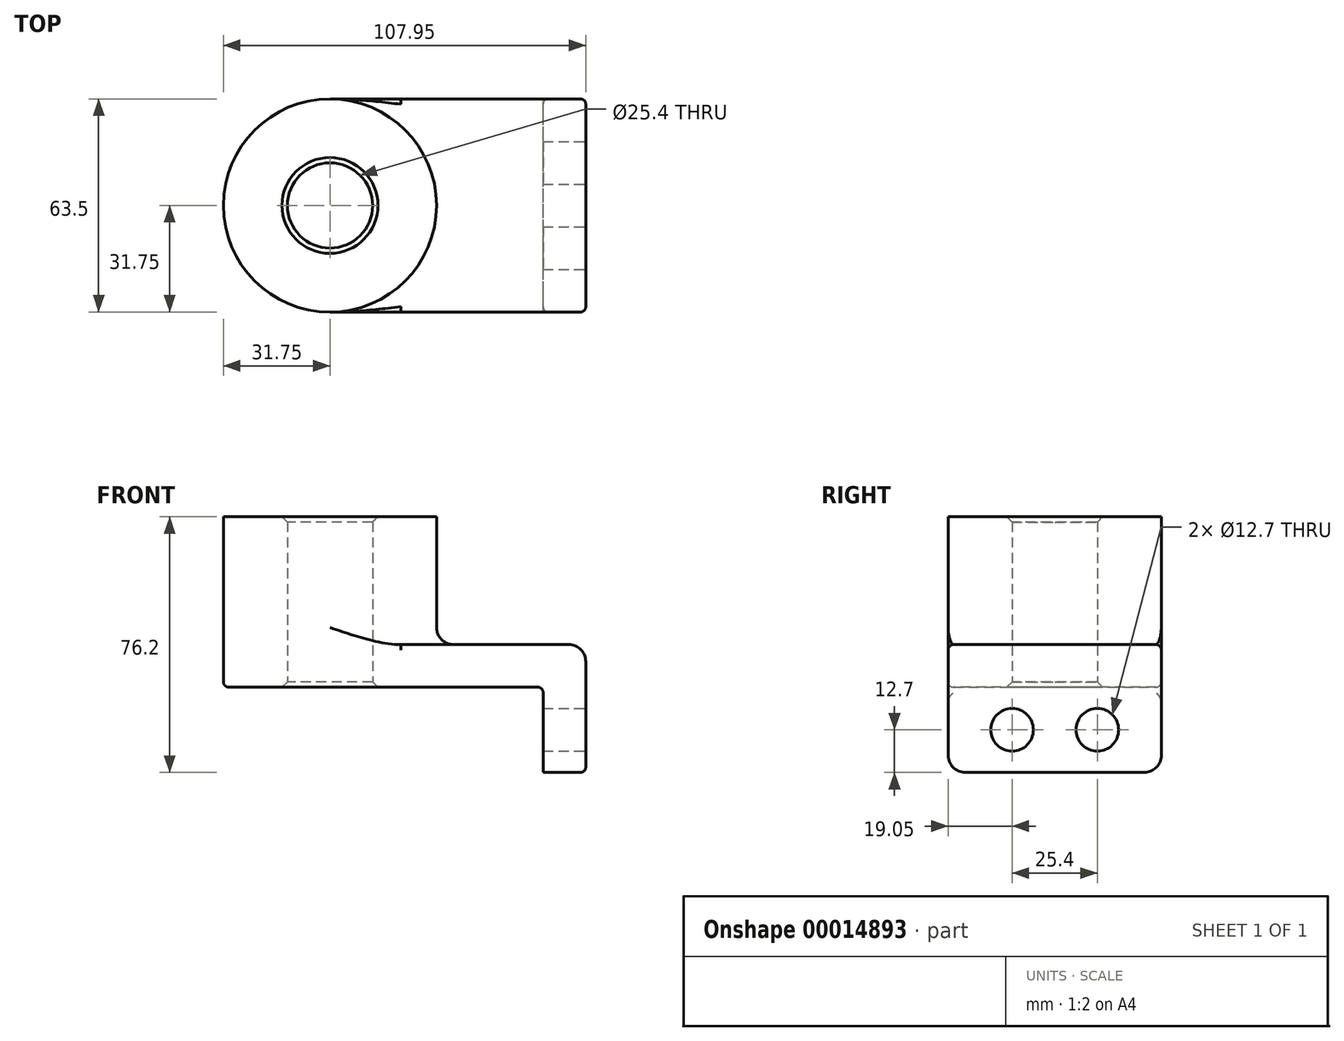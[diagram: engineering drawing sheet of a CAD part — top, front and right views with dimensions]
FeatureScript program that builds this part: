
annotation { "Feature Type Name" : "Feature", "Feature Type Description" : "" }
export const myFeature = defineFeature(function(context is Context, id is Id, definition is map)
    precondition{}
    {
        {
            var Q0;
            Q0=qCreatedBy(makeId("Top.planeOp"),FACE);
            var sketch = newSketch(context, id + "F0", { "sketchPlane" : qUnion([Q0])});
            skLineSegment(sketch, "E0.rect.bottom", {"start": v(-38.1, 31.75) * mm, "end": v(38.1, 31.75) * mm});
            skLineSegment(sketch, "E0.rect.top", {"start": v(-38.1, -31.75) * mm, "end": v(38.1, -31.75) * mm});
            skLineSegment(sketch, "E0.rect.left", {"start": v(-38.1, 31.75) * mm, "end": v(-38.1, -31.75) * mm});
            skLineSegment(sketch, "E0.rect.right", {"start": v(38.1, 31.75) * mm, "end": v(38.1, -31.75) * mm});
            skPoint(sketch, "E0.rect.middle", {"position": v(0, 0) * mm});
            skCircle(sketch, "E1", {"center": v(-38.1, 0) * mm, "radius": 31.75 * mm});
            skCircle(sketch, "E2", {"center": v(-38.1, 0) * mm, "radius": 12.7 * mm});
            skSolve(sketch);
        }
        {
            var Q0;
            Q0 = qSketchRegion(id + "F0", true);
            extrude(context, id + "F1", {"entities" : qUnion([Q0]), "depth" : 12.7 * mm});
        }
        {
            var Q0;
            {var subQ0=sQuery(id+"F0.wireOp",EDGE,"E2");var subQ1=sQuery(id+"F0.wireOp",EDGE,"E0.rect.left");var subQ3=makeQuery(id+"F0.imprint","INTERSECT",VERTEX,{"disambiguationData":[OD(0.0)],"derivedFrom":[subQ1,subQ0]});Q0=makeQuery(id+"F0.imprint","IMPRINT",FACE,{"disambiguationData":[TD([[makeQuery(id+"F0.imprint","IMPRINT",EDGE,{"disambiguationData":[TD([[subQ3,-1.0]])],"derivedFrom":subQ0}),-1.0]])]});}
            var Q1;
            {var subQ0=sQuery(id+"F0.wireOp",EDGE,"E2");var subQ1=sQuery(id+"F0.wireOp",EDGE,"E0.rect.left");var subQ3=makeQuery(id+"F0.imprint","INTERSECT",VERTEX,{"disambiguationData":[OD(0.0)],"derivedFrom":[subQ1,subQ0]});Q1=makeQuery(id+"F0.imprint","IMPRINT",FACE,{"disambiguationData":[TD([[makeQuery(id+"F0.imprint","IMPRINT",EDGE,{"disambiguationData":[TD([[subQ3,1.0]])],"derivedFrom":subQ0}),-1.0]])]});}
            extrude(context, id + "F2", {"entities" : qUnion([Q0, Q1]), "operationType" : NewBodyOperationType.ADD, "depth" : 50.8 * mm});
        }
        {
            var Q0;
            Q0=makeQuery(id+"F1.opExtrude","SWEPT_FACE",FACE,{"disambiguationData":[OSD([sQuery(id+"F0.wireOp",EDGE,"E0.rect.right")])]});
            var sketch = newSketch(context, id + "F3", { "sketchPlane" : qUnion([Q0])});
            skLineSegment(sketch, "E3.bottom", {"start": v(-31.75, 12.7) * mm, "end": v(31.75, 12.7) * mm});
            skLineSegment(sketch, "E3.top", {"start": v(-31.75, -25.4) * mm, "end": v(31.75, -25.4) * mm});
            skLineSegment(sketch, "E3.left", {"start": v(-31.75, 12.7) * mm, "end": v(-31.75, -25.4) * mm});
            skLineSegment(sketch, "E3.right", {"start": v(31.75, 12.7) * mm, "end": v(31.75, -25.4) * mm});
            skCircle(sketch, "E4", {"center": v(-12.7, -12.7) * mm, "radius": 6.35 * mm});
            skLineSegment(sketch, "E5", {"start": v(0, -3.05) * mm, "end": v(0, -25.65) * mm});
            skCircle(sketch, "E6.MirrorC", {"center": v(12.7, -12.7) * mm, "radius": 6.35 * mm});
            skSolve(sketch);
        }
        {
            var Q0;
            Q0 = qSketchRegion(id + "F3", true);
            extrude(context, id + "F4", {"entities" : qUnion([Q0]), "operationType" : NewBodyOperationType.ADD, "oppositeDirection" : true, "depth" : 12.7 * mm});
        }
        {
            var Q0;
            {var subQ0=sQuery(id+"F0.wireOp",EDGE,"E1");Q0=makeQuery(id+"F2.boolean.opBoolean","INTERSECT",EDGE,{"derivedFrom":[makeQuery(id+"F1.opExtrude","CAP_FACE",FACE,{"disambiguationData":[OSD([sQuery(id+"F0.wireOp",EDGE,"E0.rect.bottom"),sQuery(id+"F0.wireOp",EDGE,"E0.rect.top"),sQuery(id+"F0.wireOp",EDGE,"E0.rect.right"),subQ0,sQuery(id+"F0.wireOp",EDGE,"E2")])],"isStart":false}),makeQuery(id+"F2.opExtrude","SWEPT_FACE",FACE,{"disambiguationData":[OSD([subQ0])]})]});}
            var Q1;
            Q1=makeQuery(id+"F1.opExtrude","CAP_EDGE",EDGE,{"disambiguationData":[OSD([sQuery(id+"F0.wireOp",EDGE,"E0.rect.right")])],"isStart":false});
            var Q2;
            Q2=makeQuery(id+"F4.opExtrude","SWEPT_EDGE",EDGE,{"disambiguationData":[OSD([sQuery(id+"F3.wireOp",EDGE,"E3.top"),sQuery(id+"F3.wireOp",EDGE,"E3.left")])]});
            var Q3;
            Q3=makeQuery(id+"F4.opExtrude","SWEPT_EDGE",EDGE,{"disambiguationData":[OSD([sQuery(id+"F3.wireOp",EDGE,"E3.top"),sQuery(id+"F3.wireOp",EDGE,"E3.right")])]});
            fillet(context, id + "F5", {"entities" : qUnion([Q0, Q1, Q2, Q3]), "radius" : 5.08 * mm, "tangentPropagation" : true, "allowEdgeOverflow" : false});
        }
        {
            var Q0;
            Q0=makeQuery(id+"F1.opExtrude","CAP_EDGE",EDGE,{"disambiguationData":[OSD([sQuery(id+"F0.wireOp",EDGE,"E0.rect.top")])],"isStart":false});
            var Q1;
            Q1=makeQuery(id+"F1.opExtrude","CAP_EDGE",EDGE,{"disambiguationData":[OSD([sQuery(id+"F0.wireOp",EDGE,"E0.rect.top")])],"isStart":true});
            var Q2;
            Q2=makeQuery(id+"F4.boolean.opBoolean","INTERSECT",EDGE,{"derivedFrom":[makeQuery(id+"F1.opExtrude","CAP_FACE",FACE,{"disambiguationData":[OSD([sQuery(id+"F0.wireOp",EDGE,"E0.rect.bottom"),sQuery(id+"F0.wireOp",EDGE,"E0.rect.top"),sQuery(id+"F0.wireOp",EDGE,"E0.rect.right"),sQuery(id+"F0.wireOp",EDGE,"E1"),sQuery(id+"F0.wireOp",EDGE,"E2")])],"isStart":true}),makeQuery(id+"F4.opExtrude","CAP_FACE",FACE,{"disambiguationData":[OSD([sQuery(id+"F3.wireOp",EDGE,"E3.bottom"),sQuery(id+"F3.wireOp",EDGE,"E3.top"),sQuery(id+"F3.wireOp",EDGE,"E3.left"),sQuery(id+"F3.wireOp",EDGE,"E3.right"),sQuery(id+"F3.wireOp",EDGE,"E4"),sQuery(id+"F3.wireOp",EDGE,"E6.MirrorC")])],"isStart":false})]});
            fillet(context, id + "F6", {"entities" : qUnion([Q0, Q1, Q2]), "radius" : 1.59 * mm, "tangentPropagation" : true, "allowEdgeOverflow" : false});
        }
        {
            var Q0;
            {var subQ0=sQuery(id+"F0.wireOp",EDGE,"E2");Q0=makeQuery(id+"F2.boolean.opBoolean","MERGE",FACE,{"derivedFrom":[makeQuery(id+"F1.opExtrude","SWEPT_FACE",FACE,{"disambiguationData":[OSD([subQ0])]}),makeQuery(id+"F2.opExtrude","SWEPT_FACE",FACE,{"disambiguationData":[OSD([subQ0])]})]});}
            chamfer(context, id + "F7", {"entities" : qUnion([Q0]), "width" : 1.59 * mm, "tangentPropagation" : true});
        }
    });
